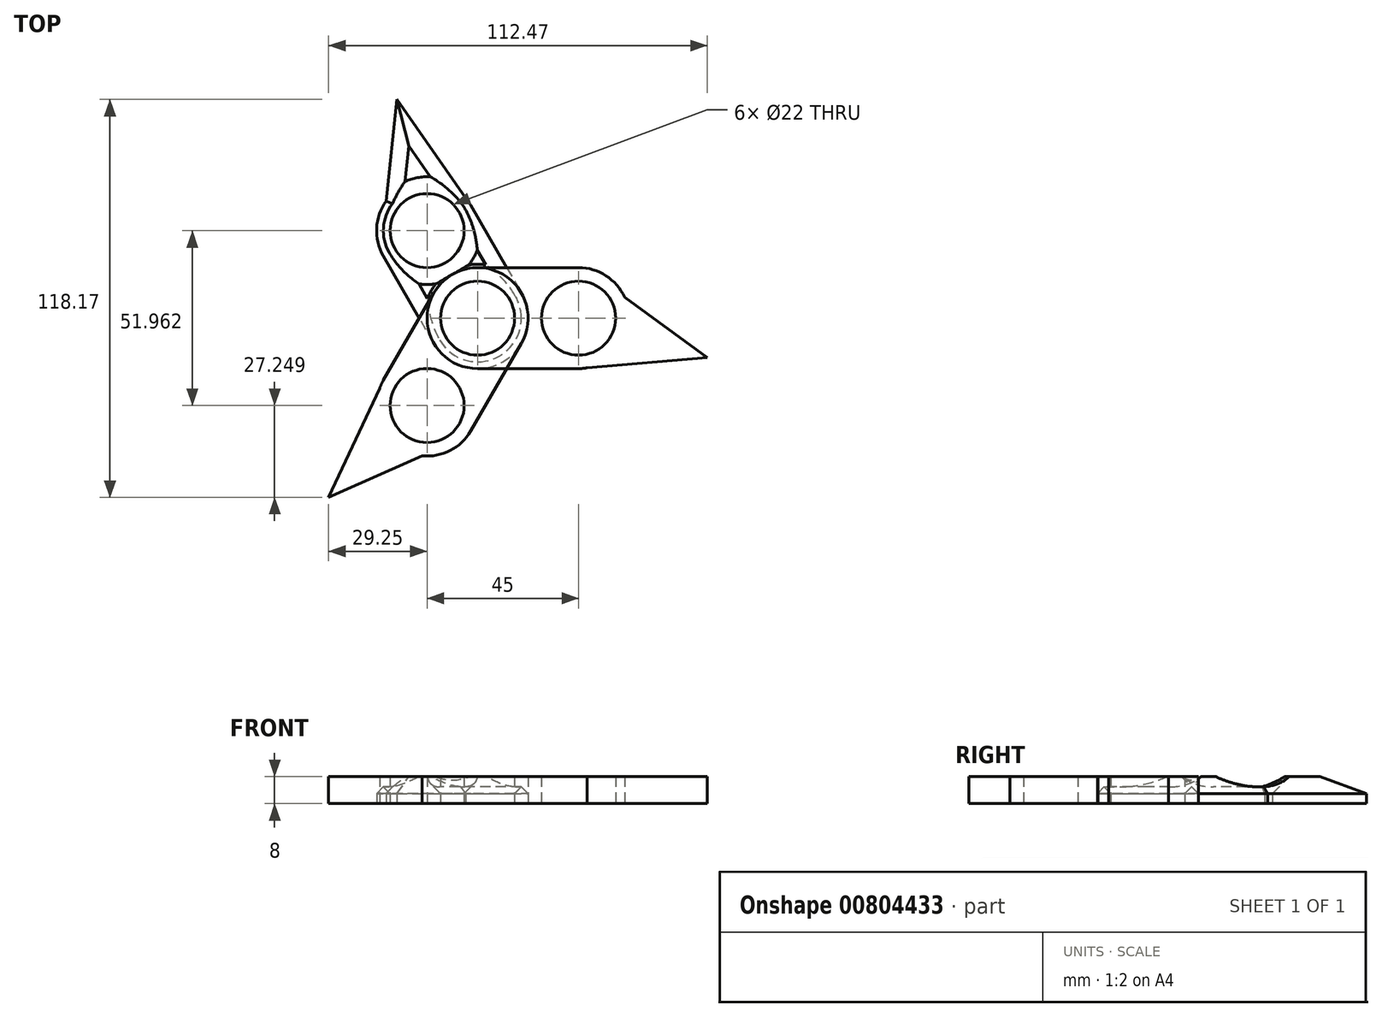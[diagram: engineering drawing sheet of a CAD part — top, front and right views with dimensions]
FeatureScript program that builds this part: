
annotation { "Feature Type Name" : "Feature", "Feature Type Description" : "" }
export const myFeature = defineFeature(function(context is Context, id is Id, definition is map)
    precondition{}
    {
        {
            var Q0;
            Q0=qCreatedBy(makeId("Top.planeOp"),FACE);
            var sketch = newSketch(context, id + "F0", { "sketchPlane" : qUnion([Q0])});
            skCircle(sketch, "E0", {"center": v(0, 0) * mm, "radius": 11 * mm});
            skCircle(sketch, "E1", {"center": v(0, 0) * mm, "radius": 15 * mm});
            skLineSegment(sketch, "E2", {"start": v(0, 0) * mm, "end": v(30, 0) * mm, "construction": true});
            skCircle(sketch, "E3", {"center": v(30, 0) * mm, "radius": 11 * mm});
            skCircle(sketch, "E4", {"center": v(30, 0) * mm, "radius": 15 * mm});
            skLineSegment(sketch, "E5", {"start": v(0, 15) * mm, "end": v(30, 15) * mm});
            skLineSegment(sketch, "E6", {"start": v(0, -15) * mm, "end": v(30, -15) * mm});
            skLineSegment(sketch, "E7", {"start": v(31.05, 15.36) * mm, "end": v(68.22, -11.7) * mm});
            skLineSegment(sketch, "E8", {"start": v(68.22, -11.7) * mm, "end": v(30, -15) * mm});
            skSolve(sketch);
        }
        {
            var Q0;
            Q0=qSketchRegion(id+"F0",true);
            extrude(context, id + "F1", {"entities" : qUnion([Q0]), "depth" : 8 * mm, "offsetDistance" : 25 * mm});
        }
        {
            var Q0;
            Q0=qCreatedBy(makeId("Front.planeOp"),FACE);
            var sketch = newSketch(context, id + "F2", { "sketchPlane" : qUnion([Q0])});
            skLineSegment(sketch, "E9", {"start": v(0, 0) * mm, "end": v(0, 51.3) * mm, "construction": true});
            skSolve(sketch);
        }
        {
            var Q0;
            Q0=makeQuery(id+"F1.opExtrude","SWEPT_BODY",BODY,{"disambiguationData":[OSD([sQuery(id+"F0.wireOp",EDGE,"E0"),sQuery(id+"F0.wireOp",EDGE,"E1"),sQuery(id+"F0.wireOp",EDGE,"E3"),sQuery(id+"F0.wireOp",EDGE,"E4"),sQuery(id+"F0.wireOp",EDGE,"E5"),sQuery(id+"F0.wireOp",EDGE,"E6")])]});
            var Q1;
            Q1=sQuery(id+"F2.wireOp",EDGE,"E9");
            circularPattern(context, id + "F3", {"entities" : qUnion([Q0]), "axis" : qUnion([Q1]), "angle" : 360 * degree, "instanceCount" : 3, "equalSpace" : true});
        }
        {
            var Q0;
            Q0=makeQuery(id+"F3.opPattern","COPY",FACE,{"derivedFrom":makeQuery(id+"F1.opExtrude","CAP_FACE",FACE,{"disambiguationData":[OSD([sQuery(id+"F0.wireOp",EDGE,"E0"),sQuery(id+"F0.wireOp",EDGE,"E1"),sQuery(id+"F0.wireOp",EDGE,"E3"),sQuery(id+"F0.wireOp",EDGE,"E4"),sQuery(id+"F0.wireOp",EDGE,"E5"),sQuery(id+"F0.wireOp",EDGE,"E6"),sQuery(id+"F0.wireOp",EDGE,"E7"),sQuery(id+"F0.wireOp",EDGE,"E8")])],"isStart":false}),"instanceName":"1"});
            chamfer(context, id + "F4", {"entities" : qUnion([Q0]), "width" : 5 * mm, "tangentPropagation" : true});
        }
    });
